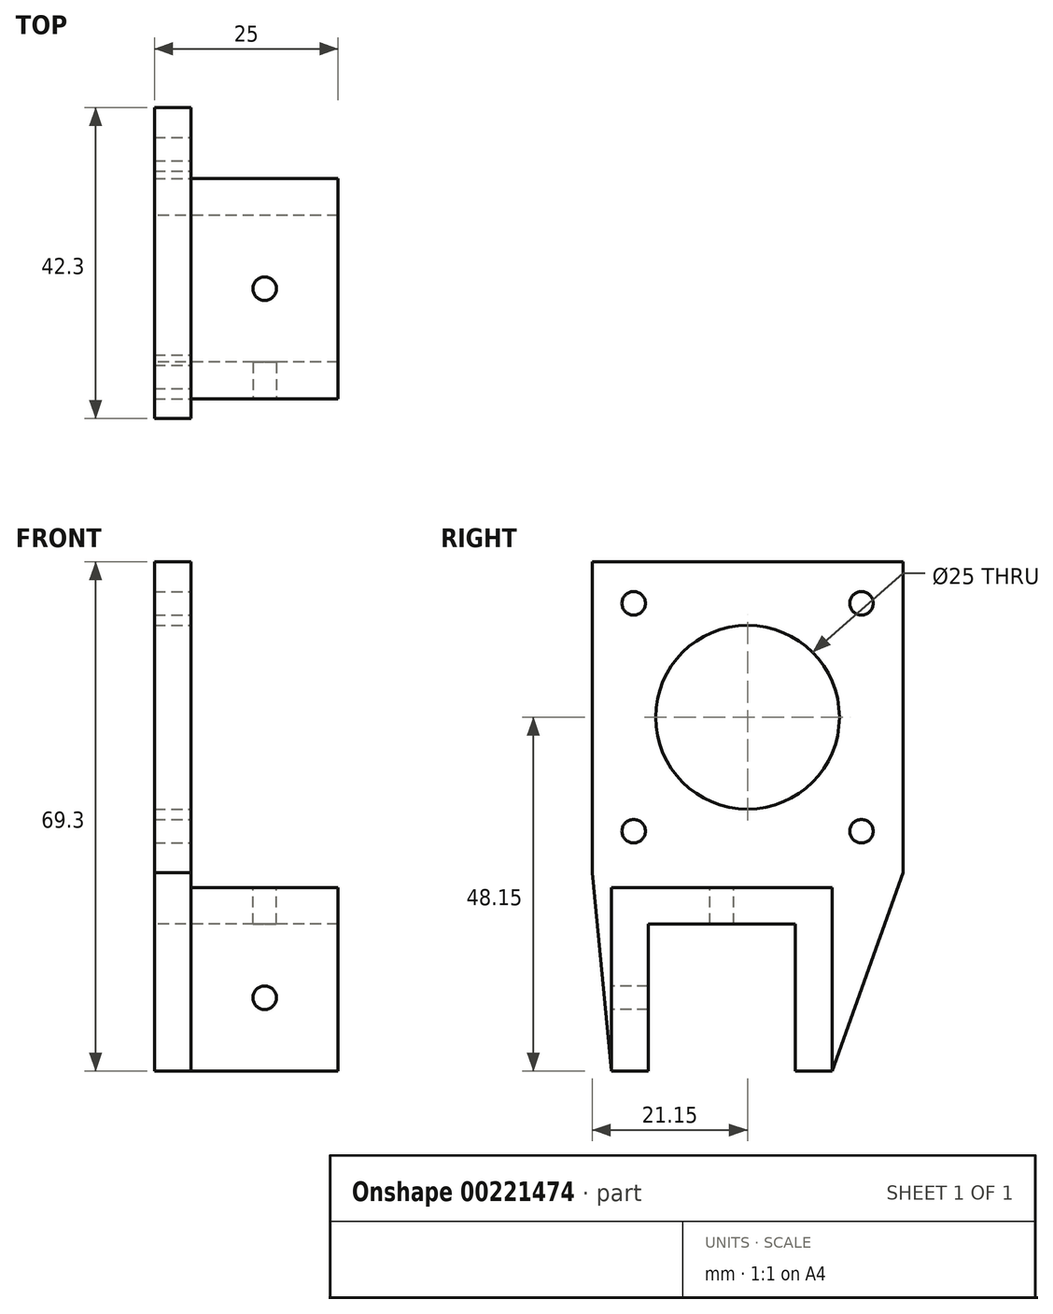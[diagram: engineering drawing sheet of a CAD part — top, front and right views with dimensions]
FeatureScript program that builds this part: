
annotation { "Feature Type Name" : "Feature", "Feature Type Description" : "" }
export const myFeature = defineFeature(function(context is Context, id is Id, definition is map)
    precondition{}
    {
        {
            var Q0;
            Q0=qCreatedBy(makeId("Front.planeOp"),FACE);
            var sketch = newSketch(context, id + "F0", { "sketchPlane" : qUnion([Q0])});
            skLineSegment(sketch, "E0.bottom", {"start": v(0, 0) * mm, "end": v(20, 0) * mm});
            skLineSegment(sketch, "E0.top", {"start": v(0, 25) * mm, "end": v(20, 25) * mm});
            skLineSegment(sketch, "E0.left", {"start": v(0, 0) * mm, "end": v(0, 25) * mm});
            skLineSegment(sketch, "E0.right", {"start": v(20, 0) * mm, "end": v(20, 25) * mm});
            skPoint(sketch, "E1.centerSnap0", {"position": v(0, 12.5) * mm});
            skPoint(sketch, "E1.centerSnap1", {"position": v(10, 0) * mm});
            skSolve(sketch);
        }
        {
            var Q0;
            Q0=makeQuery(id+"F0.imprint","IMPRINT",FACE,{"disambiguationData":[TD([[makeQuery(id+"F0.imprint","IMPRINT",EDGE,{"derivedFrom":sQuery(id+"F0.wireOp",EDGE,"E0.bottom")}),1.0]])]});
            extrude(context, id + "F1", {"entities" : qUnion([Q0]), "depth" : 5 * mm});
        }
        {
            var Q0;
            Q0=makeQuery(id+"F1.opExtrude","CAP_FACE",FACE,{"disambiguationData":[OSD([sQuery(id+"F0.wireOp",EDGE,"E0.bottom"),sQuery(id+"F0.wireOp",EDGE,"E0.top"),sQuery(id+"F0.wireOp",EDGE,"E0.left"),sQuery(id+"F0.wireOp",EDGE,"E0.right"),sQuery(id+"F0.wireOp",EDGE,"E1")])],"isStart":true});
            var sketch = newSketch(context, id + "F2", { "sketchPlane" : qUnion([Q0])});
            skLineSegment(sketch, "E2.bottom", {"start": v(-20, 25) * mm, "end": v(0, 25) * mm});
            skLineSegment(sketch, "E2.top", {"start": v(-20, 20) * mm, "end": v(0, 20) * mm});
            skLineSegment(sketch, "E2.left", {"start": v(-20, 25) * mm, "end": v(-20, 20) * mm});
            skLineSegment(sketch, "E2.right", {"start": v(0, 25) * mm, "end": v(0, 20) * mm});
            skSolve(sketch);
        }
        {
            var Q0;
            Q0=makeQuery(id+"F2.imprint","IMPRINT",FACE,{"disambiguationData":[TD([[makeQuery(id+"F2.imprint","IMPRINT",EDGE,{"derivedFrom":sQuery(id+"F2.wireOp",EDGE,"E2.bottom")}),1.0]])]});
            extrude(context, id + "F3", {"entities" : qUnion([Q0]), "operationType" : NewBodyOperationType.ADD, "depth" : 20 * mm});
        }
        {
            var Q0;
            Q0=makeQuery(id+"F1.opExtrude","CAP_FACE",FACE,{"disambiguationData":[OSD([sQuery(id+"F0.wireOp",EDGE,"E0.bottom"),sQuery(id+"F0.wireOp",EDGE,"E0.top"),sQuery(id+"F0.wireOp",EDGE,"E0.left"),sQuery(id+"F0.wireOp",EDGE,"E0.right")])],"isStart":true});
            var sketch = newSketch(context, id + "F4", { "sketchPlane" : qUnion([Q0])});
            skPoint(sketch, "E3", {"position": v(-10, 10) * mm});
            skPoint(sketch, "E3.positionSnap0", {"position": v(-10, 0) * mm});
            skPoint(sketch, "E3.positionSnap1", {"position": v(0, 10) * mm});
            skSolve(sketch);
        }
        {
            var Q0;
            Q0=makeQuery(id+"F3.opExtrude","SWEPT_FACE",FACE,{"disambiguationData":[OSD([sQuery(id+"F2.wireOp",EDGE,"E2.top")])]});
            var sketch = newSketch(context, id + "F5", { "sketchPlane" : qUnion([Q0])});
            skPoint(sketch, "E4", {"position": v(10, -10) * mm});
            skPoint(sketch, "E4.positionSnap0", {"position": v(10, 0) * mm});
            skPoint(sketch, "E4.positionSnap1", {"position": v(0, -10) * mm});
            skSolve(sketch);
        }
        {
            var Q0;
            Q0=sQuery(id+"F4.wireOp",VERTEX,"E3");
            var Q1;
            Q1=sQuery(id+"F5.wireOp",VERTEX,"E4");
            var Q2;
            Q2=makeQuery(id+"F1.opExtrude","SWEPT_BODY",BODY,{"disambiguationData":[OSD([sQuery(id+"F0.wireOp",EDGE,"E0.bottom"),sQuery(id+"F0.wireOp",EDGE,"E0.top"),sQuery(id+"F0.wireOp",EDGE,"E0.left"),sQuery(id+"F0.wireOp",EDGE,"E0.right")])]});
            hole(context, id + "F6", {"style" : HoleStyle.SIMPLE, "endStyle" : HoleEndStyle.THROUGH, "holeDiameter" : 3.2 * mm, "locations" : qUnion([Q0, Q1]), "scope" : qUnion([Q2]), "isTappedThrough" : true});
        }
        {
            var Q0;
            Q0=makeQuery(id+"F3.boolean.opBoolean","MERGE",FACE,{"derivedFrom":[makeQuery(id+"F1.opExtrude","SWEPT_FACE",FACE,{"disambiguationData":[OSD([sQuery(id+"F0.wireOp",EDGE,"E0.top")])]}),makeQuery(id+"F3.opExtrude","SWEPT_FACE",FACE,{"disambiguationData":[OSD([sQuery(id+"F2.wireOp",EDGE,"E2.bottom")])]})]});
            var sketch = newSketch(context, id + "F7", { "sketchPlane" : qUnion([Q0])});
            skLineSegment(sketch, "E5.bottom", {"start": v(0, 20) * mm, "end": v(20, 20) * mm});
            skLineSegment(sketch, "E5.top", {"start": v(0, 25) * mm, "end": v(20, 25) * mm});
            skLineSegment(sketch, "E5.left", {"start": v(0, 20) * mm, "end": v(0, 25) * mm});
            skLineSegment(sketch, "E5.right", {"start": v(20, 20) * mm, "end": v(20, 25) * mm});
            skSolve(sketch);
        }
        {
            var Q0;
            Q0=makeQuery(id+"F7.imprint","IMPRINT",FACE,{"disambiguationData":[TD([[makeQuery(id+"F7.imprint","IMPRINT",EDGE,{"derivedFrom":sQuery(id+"F7.wireOp",EDGE,"E5.bottom")}),1.0]])]});
            extrude(context, id + "F8", {"entities" : qUnion([Q0]), "operationType" : NewBodyOperationType.ADD, "oppositeDirection" : true, "depth" : 25 * mm});
        }
        {
            var Q0;
            Q0=makeQuery(id+"F3.boolean.opBoolean","MERGE",FACE,{"derivedFrom":[makeQuery(id+"F1.opExtrude","SWEPT_FACE",FACE,{"disambiguationData":[OSD([sQuery(id+"F0.wireOp",EDGE,"E0.left")])]}),makeQuery(id+"F3.opExtrude","SWEPT_FACE",FACE,{"disambiguationData":[OSD([sQuery(id+"F2.wireOp",EDGE,"E2.right")])]})]});
            var sketch = newSketch(context, id + "F9", { "sketchPlane" : qUnion([Q0])});
            skLineSegment(sketch, "E6.bottom", {"start": v(2, 63.65) * mm, "end": v(-29, 63.65) * mm, "construction": true});
            skLineSegment(sketch, "E6.top", {"start": v(2, 32.65) * mm, "end": v(-29, 32.65) * mm, "construction": true});
            skLineSegment(sketch, "E6.left", {"start": v(2, 63.65) * mm, "end": v(2, 32.65) * mm, "construction": true});
            skLineSegment(sketch, "E6.right", {"start": v(-29, 63.65) * mm, "end": v(-29, 32.65) * mm, "construction": true});
            skCircle(sketch, "E7", {"center": v(2, 63.65) * mm, "radius": 1.6 * mm});
            skCircle(sketch, "E8", {"center": v(-29, 63.65) * mm, "radius": 1.6 * mm});
            skCircle(sketch, "E9", {"center": v(-29, 32.65) * mm, "radius": 1.6 * mm});
            skCircle(sketch, "E10", {"center": v(2, 32.65) * mm, "radius": 1.6 * mm});
            skCircle(sketch, "E11", {"center": v(-13.5, 48.15) * mm, "radius": 12.5 * mm});
            skPoint(sketch, "E11.centerSnap0", {"position": v(2, 48.15) * mm});
            skPoint(sketch, "E11.centerSnap1", {"position": v(-13.5, 63.65) * mm});
            skLineSegment(sketch, "E12.bottom", {"start": v(7.65, 69.3) * mm, "end": v(-34.65, 69.3) * mm});
            skLineSegment(sketch, "E12.top", {"start": v(7.65, 27) * mm, "end": v(-34.65, 27) * mm, "construction": true});
            skLineSegment(sketch, "E12.left", {"start": v(7.65, 69.3) * mm, "end": v(7.65, 27) * mm});
            skLineSegment(sketch, "E12.right", {"start": v(-34.65, 69.3) * mm, "end": v(-34.65, 27) * mm});
            skLineSegment(sketch, "E13", {"start": v(-20, 20) * mm, "end": v(0, 20) * mm});
            skLineSegment(sketch, "E14", {"start": v(0, 20) * mm, "end": v(0, 0) * mm});
            skLineSegment(sketch, "E15", {"start": v(0, 0) * mm, "end": v(5, 0) * mm});
            skLineSegment(sketch, "E16", {"start": v(5, 0) * mm, "end": v(7.65, 27) * mm});
            skLineSegment(sketch, "E17", {"start": v(-34.65, 27) * mm, "end": v(-25, 0) * mm});
            skLineSegment(sketch, "E18", {"start": v(-25, 0) * mm, "end": v(-20, 0) * mm});
            skLineSegment(sketch, "E19", {"start": v(-20, 0) * mm, "end": v(-20, 20) * mm});
            skSolve(sketch);
        }
        {
            var Q0;
            Q0 = qSketchRegion(id + "F9", true);
            extrude(context, id + "F10", {"entities" : qUnion([Q0]), "operationType" : NewBodyOperationType.ADD, "depth" : 5 * mm});
        }
    });
